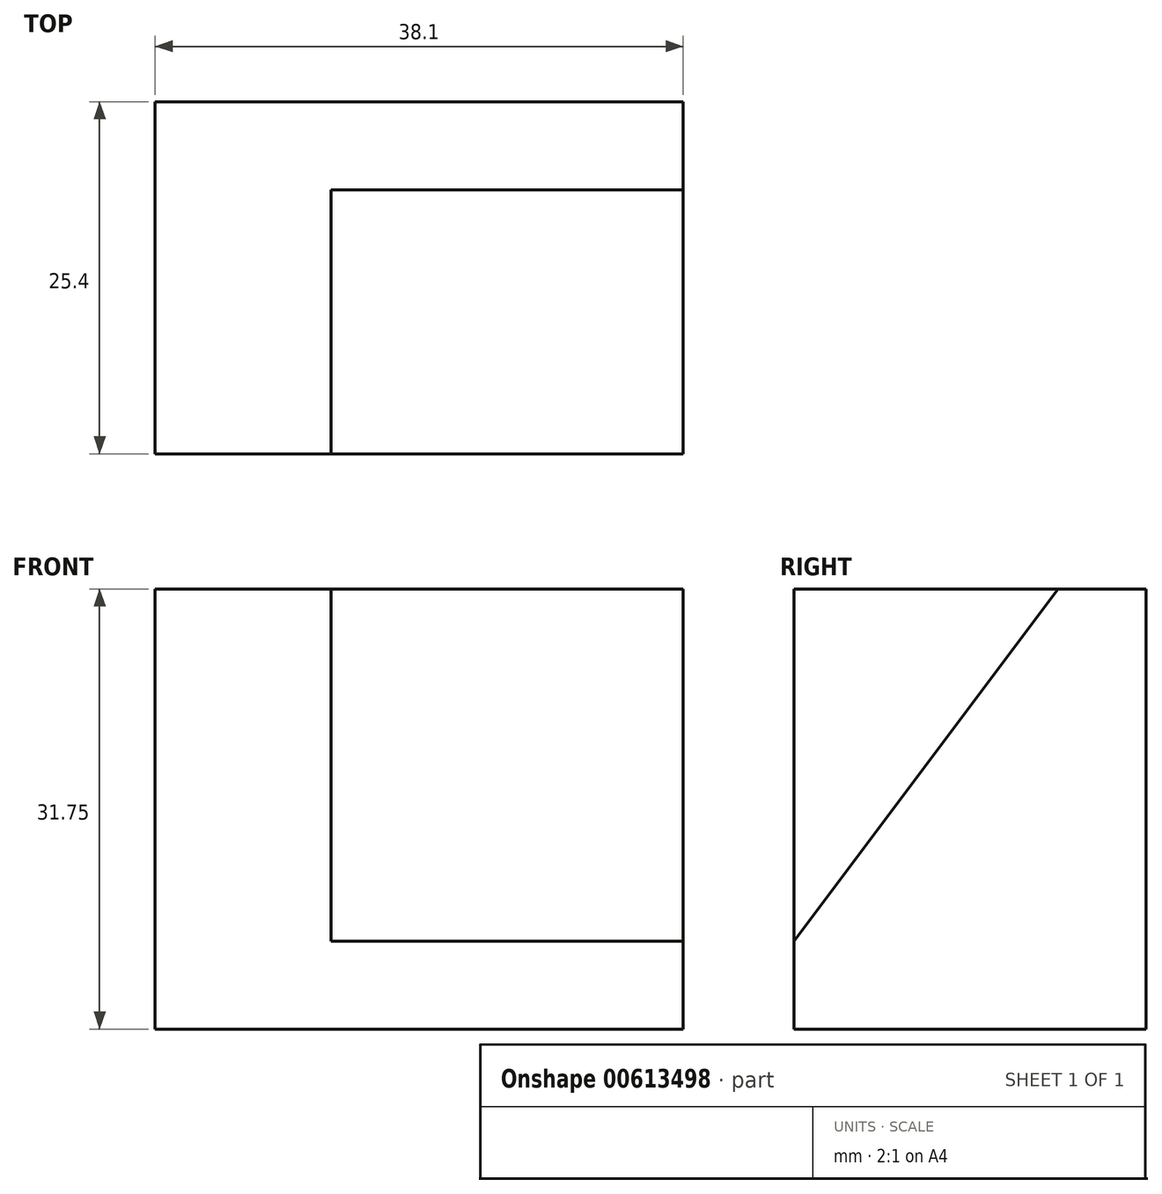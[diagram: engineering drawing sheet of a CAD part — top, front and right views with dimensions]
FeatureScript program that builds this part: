
annotation { "Feature Type Name" : "Feature", "Feature Type Description" : "" }
export const myFeature = defineFeature(function(context is Context, id is Id, definition is map)
    precondition{}
    {
        {
            var Q0;
            Q0=qCreatedBy(makeId("Right.planeOp"),FACE);
            var sketch = newSketch(context, id + "F0", { "sketchPlane" : qUnion([Q0])});
            skLineSegment(sketch, "E0", {"start": v(25.4, 0) * mm, "end": v(0, 0) * mm});
            skLineSegment(sketch, "E1", {"start": v(0, 0) * mm, "end": v(0, 31.75) * mm});
            skLineSegment(sketch, "E2", {"start": v(0, 31.75) * mm, "end": v(25.4, 31.75) * mm});
            skLineSegment(sketch, "E3", {"start": v(25.4, 31.75) * mm, "end": v(25.4, 0) * mm});
            skSolve(sketch);
        }
        {
            var Q0;
            Q0=makeQuery(id+"F0.imprint","IMPRINT",FACE,{"disambiguationData":[TD([[makeQuery(id+"F0.imprint","IMPRINT",EDGE,{"derivedFrom":sQuery(id+"F0.wireOp",EDGE,"E0")}),-1.0]])]});
            extrude(context, id + "F1", {"entities" : qUnion([Q0]), "depth" : 38.1 * mm, "offsetDistance" : 25.4 * mm});
        }
        {
            var Q0;
            Q0=makeQuery(id+"F1.opExtrude","CAP_FACE",FACE,{"disambiguationData":[OSD([sQuery(id+"F0.wireOp",EDGE,"E0"),sQuery(id+"F0.wireOp",EDGE,"E1"),sQuery(id+"F0.wireOp",EDGE,"E2"),sQuery(id+"F0.wireOp",EDGE,"E3")])],"isStart":false});
            var sketch = newSketch(context, id + "F2", { "sketchPlane" : qUnion([Q0])});
            skLineSegment(sketch, "E4", {"start": v(0, 0) * mm, "end": v(0, 6.35) * mm});
            skLineSegment(sketch, "E5", {"start": v(0, 31.75) * mm, "end": v(19.05, 31.75) * mm});
            skLineSegment(sketch, "E6", {"start": v(19.05, 31.75) * mm, "end": v(0, 6.35) * mm});
            skSolve(sketch);
        }
        {
            var Q0;
            {var subQ0=sQuery(id+"F2.wireOp",EDGE,"E5");Q0=makeQuery(id+"F2.imprint","IMPRINT",FACE,{"disambiguationData":[TD([[makeQuery(id+"F2.imprint","IMPRINT",EDGE,{"derivedFrom":subQ0}),-1.0]])]});}
            extrude(context, id + "F3", {"entities" : qUnion([Q0]), "operationType" : NewBodyOperationType.REMOVE, "oppositeDirection" : true, "depth" : 25.4 * mm, "offsetDistance" : 25.4 * mm});
        }
    });
